# Revit family: equip-faucet-elkay-lk943C
name_source: partatom
category: Plumbing Fixtures
units: mm (PartAtom-declared; Revit-internal decimal feet)

## family parameters
Always vertical = Yes
Cut with Voids When Loaded = No
OmniClass Number = 23.45.55.17
OmniClass Title = Mixing Faucets
Part Type = Normal
Room Calculation Point = No
Round Connector Dimension = Use Radius
Shared = No
Work Plane-Based = Yes

## types (1)
- equip-faucet-elkay-lk943C
    Assembly Code = D2010900
    CW Flow Rate = 3.2 GPM
    Cost = 0 $
    Default Elevation = 4' - 0"
    Description = "Faucet"
    Faucet Material = Metal - Steel - Stainless - Chrome
    HA08 N AT08 N TS08 = Yes
    HA10 n AT10 = Yes
    HW Flow Rate = 3.2 GPM
    L2 = Yes
    Manufacturer = Elkay Manufacturing"
    MasterFormat Number = 22 42 39
22 42 39
22 42 39
    MasterFormat Title = Commercial Faucets
    Model = LK943C
    Nominal Dia = 0' - 0 1/2"
    Nominal Radius = 0' - 0 1/4"
    OmniClass Code = 23.45.55.17
    OmniClass Title = Mixing Faucets
    Pre-Rinse Hose = Metal - Steel - Stainless - Chrome
    Pre-Rinse Main = Metal - Steel - Stainless - Chrome
    Pre-Rinse Sprayer = Metal - Steel - Stainless - Chrome
    Specification URL = http://www.elkayusa.com
    Stem Material = Metal - Steel
    URL = www.elkayusa.com

## geometry (parser evidence)
native form markers: Sweep x2
no freeform markers — native parametric forms only
